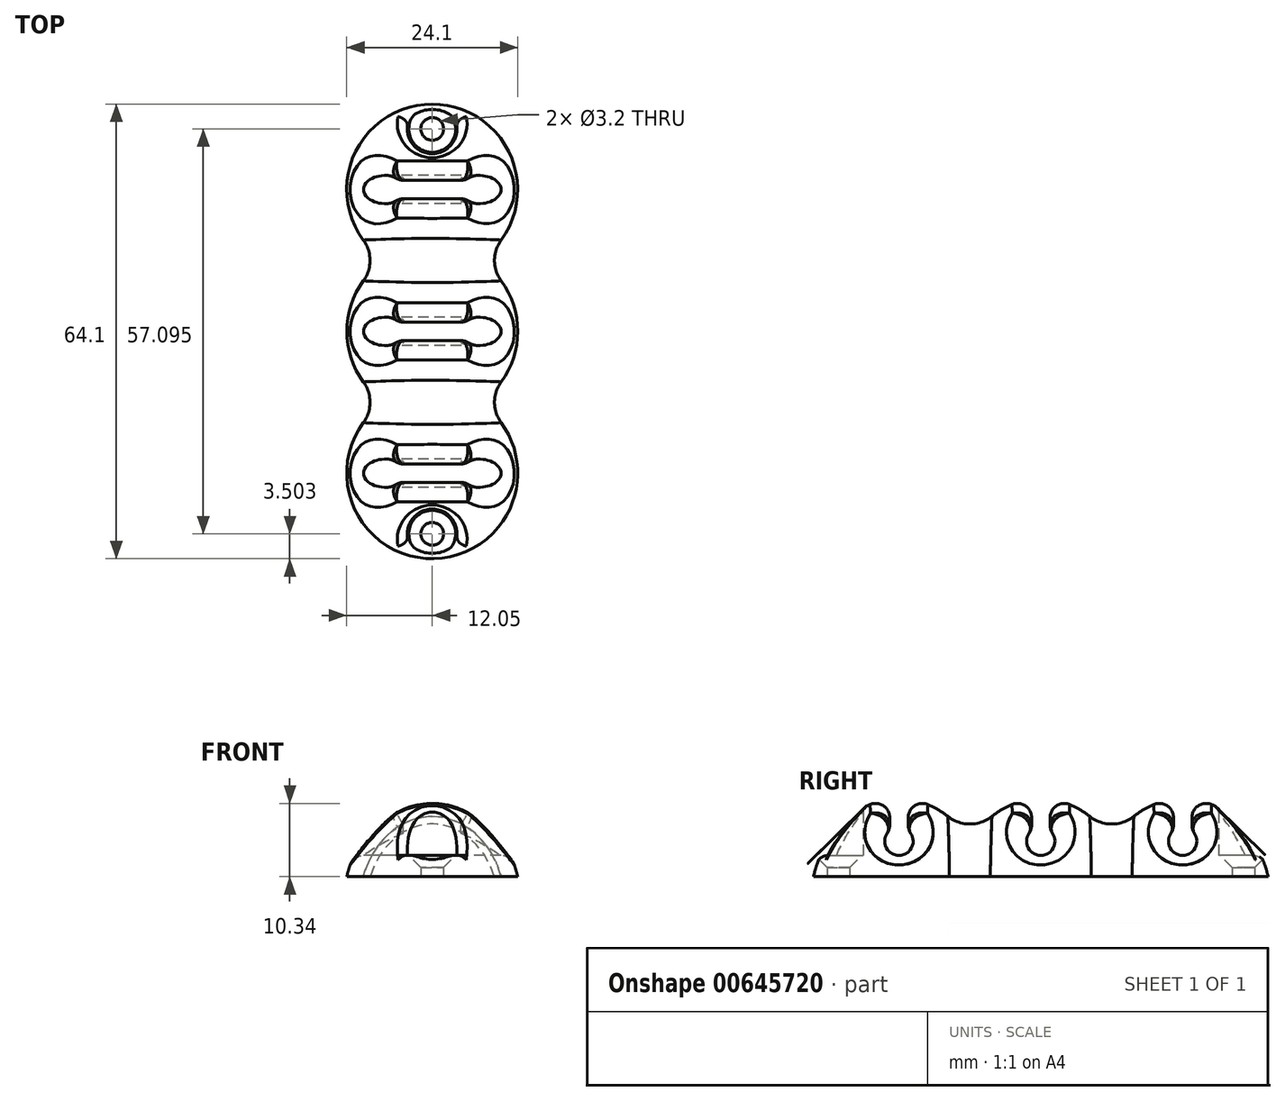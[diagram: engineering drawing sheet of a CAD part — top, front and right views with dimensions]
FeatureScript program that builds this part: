
annotation { "Feature Type Name" : "Feature", "Feature Type Description" : "" }
export const myFeature = defineFeature(function(context is Context, id is Id, definition is map)
    precondition{}
    {
        {
            var Q0;
            Q0=qCreatedBy(makeId("Right.planeOp"),FACE);
            var sketch = newSketch(context, id + "F0", { "sketchPlane" : qUnion([Q0])});
            skEllipse(sketch, "E0", {"center": v(0, -4) * mm, "majorRadius": 12.5 * mm, "minorRadius": 15 * mm, "majorAxis": v(1, 0)});
            skLineSegment(sketch, "E1.bottom", {"start": v(-40.37, 30.12) * mm, "end": v(0, 30.12) * mm});
            skLineSegment(sketch, "E1.top", {"start": v(-40.37, 0) * mm, "end": v(0, 0) * mm});
            skLineSegment(sketch, "E1.left", {"start": v(-40.37, 30.12) * mm, "end": v(-40.37, 0) * mm});
            skLineSegment(sketch, "E1.right", {"start": v(0, 30.12) * mm, "end": v(0, 0) * mm});
            skSolve(sketch);
        }
        {
            var Q0;
            {var subQ0=sQuery(id+"F0.wireOp",EDGE,"E1.top");var subQ1=sQuery(id+"F0.wireOp",EDGE,"E0");var subQ2=makeQuery(id+"F0.imprint","INTERSECT",VERTEX,{"derivedFrom":[subQ1,subQ0]});Q0=makeQuery(id+"F0.imprint","IMPRINT",FACE,{"disambiguationData":[TD([[makeQuery(id+"F0.imprint","IMPRINT",EDGE,{"disambiguationData":[TD([[subQ2,1.0]])],"derivedFrom":subQ1}),1.0]])]});}
            var Q1;
            Q1=sQuery(id+"F0.wireOp",EDGE,"E1.right");
            revolve(context, id + "F1", {"entities" : qUnion([Q0]), "axis" : qUnion([Q1]), "revolveType" : RevolveType.FULL});
        }
        {
            var Q0;
            Q0=qCreatedBy(makeId("Right.planeOp"),FACE);
            var sketch = newSketch(context, id + "F2", { "sketchPlane" : qUnion([Q0])});
            skArc(sketch, "E2", {"start": v(-1.3, 6.52) * mm, "mid": v(0, 3) * mm, "end": v(1.3, 6.52) * mm});
            skLineSegment(sketch, "E3.top", {"start": v(1.3, 24.85) * mm, "end": v(-1.3, 24.85) * mm});
            skLineSegment(sketch, "E3.left", {"start": v(1.3, 6.52) * mm, "end": v(1.3, 24.85) * mm});
            skLineSegment(sketch, "E3.right", {"start": v(-1.3, 6.52) * mm, "end": v(-1.3, 24.85) * mm});
            skPoint(sketch, "E3.middle", {"position": v(0, 15.36) * mm});
            skPoint(sketch, "E4.orphan", {"position": v(-1.3, 5.87) * mm});
            skPoint(sketch, "E5.orphan", {"position": v(1.3, 5.87) * mm});
            skSolve(sketch);
        }
        {
            var Q0;
            Q0=makeQuery(id+"F2.imprint","IMPRINT",FACE,{"disambiguationData":[TD([[makeQuery(id+"F2.imprint","IMPRINT",EDGE,{"derivedFrom":sQuery(id+"F2.wireOp",EDGE,"E2")}),1.0]])]});
            extrude(context, id + "F3", {"entities" : qUnion([Q0]), "depth" : 30 * mm, "offsetDistance" : 25 * mm, "hasSecondDirection" : true, "secondDirectionOppositeDirection" : true, "secondDirectionDepth" : 30 * mm});
        }
        {
            var Q0;
            Q0=makeQuery(id+"F3.opExtrude","SWEPT_EDGE",EDGE,{"disambiguationData":[OSD([sQuery(id+"F2.wireOp",EDGE,"E2"),sQuery(id+"F2.wireOp",EDGE,"E3.right")])]});
            var Q1;
            Q1=makeQuery(id+"F3.opExtrude","SWEPT_EDGE",EDGE,{"disambiguationData":[OSD([sQuery(id+"F2.wireOp",EDGE,"E2"),sQuery(id+"F2.wireOp",EDGE,"E3.left")])]});
            fillet(context, id + "F4", {"entities" : qUnion([Q0, Q1]), "radius" : 2 * mm, "tangentPropagation" : true, "allowEdgeOverflow" : false});
        }
        {
            var Q0;
            Q0=makeQuery(id+"F3.opExtrude","SWEPT_BODY",BODY,{"disambiguationData":[OSD([sQuery(id+"F2.wireOp",EDGE,"E2"),sQuery(id+"F2.wireOp",EDGE,"E3.top"),sQuery(id+"F2.wireOp",EDGE,"E3.left"),sQuery(id+"F2.wireOp",EDGE,"E3.right")])]});
            var Q1;
            Q1=makeQuery(id+"F1.opRevolve","SWEPT_BODY",BODY,{"disambiguationData":[OSD([sQuery(id+"F0.wireOp",EDGE,"E0"),sQuery(id+"F0.wireOp",EDGE,"E1.top"),sQuery(id+"F0.wireOp",EDGE,"E1.right")])]});
            booleanBodies(context, id + "F5", {"operationType" : BooleanOperationType.SUBTRACTION, "tools" : qUnion([Q0]), "targets" : qUnion([Q1])});
        }
        {
            var Q0;
            Q0=makeQuery(id+"F5.opBoolean","INTERSECT",EDGE,{"derivedFrom":[makeQuery(id+"F1.opRevolve","SWEPT_FACE",FACE,{"disambiguationData":[OSD([sQuery(id+"F0.wireOp",EDGE,"E0")])]}),makeQuery(id+"F3.opExtrude","SWEPT_FACE",FACE,{"disambiguationData":[OSD([sQuery(id+"F2.wireOp",EDGE,"E3.right")])]})]});
            fillet(context, id + "F6", {"entities" : qUnion([Q0]), "radius" : 2 * mm, "tangentPropagation" : true, "allowEdgeOverflow" : false});
        }
        {
            var Q0;
            Q0=makeQuery(id+"F1.opRevolve","SWEPT_BODY",BODY,{"disambiguationData":[OSD([sQuery(id+"F0.wireOp",EDGE,"E0"),sQuery(id+"F0.wireOp",EDGE,"E1.top"),sQuery(id+"F0.wireOp",EDGE,"E1.right")])]});
            transform(context, id + "F7", {"entities" : qUnion([Q0]), "transformType" : TransformType.TRANSLATION_3D, "dx" : 0 * mm, "dy" : 20 * mm, "dz" : 0 * mm, "makeCopy" : true});
        }
        {
            var Q0;
            Q0=makeQuery(id+"F7.opPattern","COPY",BODY,{"derivedFrom":makeQuery(id+"F1.opRevolve","SWEPT_BODY",BODY,{"disambiguationData":[OSD([sQuery(id+"F0.wireOp",EDGE,"E0"),sQuery(id+"F0.wireOp",EDGE,"E1.top"),sQuery(id+"F0.wireOp",EDGE,"E1.right")])]}),"instanceName":"1"});
            transform(context, id + "F8", {"entities" : qUnion([Q0]), "transformType" : TransformType.TRANSLATION_3D, "dx" : 0 * mm, "dy" : 20 * mm, "dz" : 0 * mm, "makeCopy" : true});
        }
        {
            var Q0;
            Q0=makeQuery(id+"F1.opRevolve","SWEPT_BODY",BODY,{"disambiguationData":[OSD([sQuery(id+"F0.wireOp",EDGE,"E0"),sQuery(id+"F0.wireOp",EDGE,"E1.top"),sQuery(id+"F0.wireOp",EDGE,"E1.right")])]});
            var Q1;
            Q1=makeQuery(id+"F7.opPattern","COPY",BODY,{"derivedFrom":makeQuery(id+"F1.opRevolve","SWEPT_BODY",BODY,{"disambiguationData":[OSD([sQuery(id+"F0.wireOp",EDGE,"E0"),sQuery(id+"F0.wireOp",EDGE,"E1.top"),sQuery(id+"F0.wireOp",EDGE,"E1.right")])]}),"instanceName":"1"});
            var Q2;
            Q2=makeQuery(id+"F8.opPattern","COPY",BODY,{"derivedFrom":makeQuery(id+"F7.opPattern","COPY",BODY,{"derivedFrom":makeQuery(id+"F1.opRevolve","SWEPT_BODY",BODY,{"disambiguationData":[OSD([sQuery(id+"F0.wireOp",EDGE,"E0"),sQuery(id+"F0.wireOp",EDGE,"E1.top"),sQuery(id+"F0.wireOp",EDGE,"E1.right")])]}),"instanceName":"1"}),"instanceName":"1"});
            booleanBodies(context, id + "F9", {"operationType" : BooleanOperationType.UNION, "tools" : qUnion([Q0, Q1, Q2])});
        }
        {
            var Q0;
            {var subQ0=makeQuery(id+"F1.opRevolve","SWEPT_FACE",FACE,{"disambiguationData":[OSD([sQuery(id+"F0.wireOp",EDGE,"E0")])]});Q0=makeQuery(id+"F9.opBoolean","INTERSECT",EDGE,{"derivedFrom":[subQ0,makeQuery(id+"F7.opPattern","COPY",FACE,{"derivedFrom":subQ0,"instanceName":"1"})]});}
            var Q1;
            {var subQ0=makeQuery(id+"F7.opPattern","COPY",FACE,{"derivedFrom":makeQuery(id+"F1.opRevolve","SWEPT_FACE",FACE,{"disambiguationData":[OSD([sQuery(id+"F0.wireOp",EDGE,"E0")])]}),"instanceName":"1"});Q1=makeQuery(id+"F9.opBoolean","INTERSECT",EDGE,{"derivedFrom":[subQ0,makeQuery(id+"F8.opPattern","COPY",FACE,{"derivedFrom":subQ0,"instanceName":"1"})]});}
            fillet(context, id + "F10", {"entities" : qUnion([Q0, Q1]), "radius" : 5 * mm, "tangentPropagation" : true, "allowEdgeOverflow" : false});
        }
        {
            var Q0;
            {var subQ0=makeQuery(id+"F1.opRevolve","SWEPT_FACE",FACE,{"disambiguationData":[OSD([sQuery(id+"F0.wireOp",EDGE,"E1.top")])]});var subQ1=makeQuery(id+"F7.opPattern","COPY",FACE,{"derivedFrom":subQ0,"instanceName":"1"});Q0=makeQuery(id+"F9.opBoolean","MERGE",FACE,{"derivedFrom":[subQ0,subQ1,makeQuery(id+"F8.opPattern","COPY",FACE,{"derivedFrom":subQ1,"instanceName":"1"})]});}
            var sketch = newSketch(context, id + "F11", { "sketchPlane" : qUnion([Q0])});
            skCircle(sketch, "E6", {"center": v(0, 8.55) * mm, "radius": 3.5 * mm});
            skCircle(sketch, "E7", {"center": v(0, -48.55) * mm, "radius": 3.5 * mm});
            skSolve(sketch);
        }
        {
            var Q0;
            Q0=makeQuery(id+"F11.imprint","IMPRINT",FACE,{"disambiguationData":[TD([[makeQuery(id+"F11.imprint","IMPRINT",EDGE,{"derivedFrom":sQuery(id+"F11.wireOp",EDGE,"E6")}),1.0]])]});
            var Q1;
            Q1=makeQuery(id+"F11.imprint","IMPRINT",FACE,{"disambiguationData":[TD([[makeQuery(id+"F11.imprint","IMPRINT",EDGE,{"derivedFrom":sQuery(id+"F11.wireOp",EDGE,"E7")}),1.0]])]});
            extrude(context, id + "F12", {"entities" : qUnion([Q0, Q1]), "oppositeDirection" : true, "depth" : 25 * mm, "offsetDistance" : 25 * mm});
        }
        {
            var Q0;
            Q0=makeQuery(id+"F12.opExtrude","SWEPT_BODY",BODY,{"disambiguationData":[OSD([sQuery(id+"F11.wireOp",EDGE,"E7")])]});
            var Q1;
            Q1=makeQuery(id+"F12.opExtrude","SWEPT_BODY",BODY,{"disambiguationData":[OSD([sQuery(id+"F11.wireOp",EDGE,"E6")])]});
            transform(context, id + "F13", {"entities" : qUnion([Q0, Q1]), "transformType" : TransformType.TRANSLATION_3D, "dx" : 0 * mm, "dy" : 0 * mm, "dz" : 3 * mm, "makeCopy" : false});
        }
        {
            var Q0;
            Q0=makeQuery(id+"F12.opExtrude","SWEPT_BODY",BODY,{"disambiguationData":[OSD([sQuery(id+"F11.wireOp",EDGE,"E7")])]});
            var Q1;
            Q1=makeQuery(id+"F12.opExtrude","SWEPT_BODY",BODY,{"disambiguationData":[OSD([sQuery(id+"F11.wireOp",EDGE,"E6")])]});
            var Q2;
            Q2=makeQuery(id+"F1.opRevolve","SWEPT_BODY",BODY,{"disambiguationData":[OSD([sQuery(id+"F0.wireOp",EDGE,"E0"),sQuery(id+"F0.wireOp",EDGE,"E1.top"),sQuery(id+"F0.wireOp",EDGE,"E1.right")])]});
            booleanBodies(context, id + "F14", {"operationType" : BooleanOperationType.SUBTRACTION, "tools" : qUnion([Q0, Q1]), "targets" : qUnion([Q2])});
        }
        {
            var Q0;
            Q0=makeQuery(id+"F14.opBoolean","INTERSECT",EDGE,{"derivedFrom":[makeQuery(id+"F8.opPattern","COPY",FACE,{"derivedFrom":makeQuery(id+"F7.opPattern","COPY",FACE,{"derivedFrom":makeQuery(id+"F1.opRevolve","SWEPT_FACE",FACE,{"disambiguationData":[OSD([sQuery(id+"F0.wireOp",EDGE,"E0")])]}),"instanceName":"1"}),"instanceName":"1"}),makeQuery(id+"F12.opExtrude","SWEPT_FACE",FACE,{"disambiguationData":[OSD([sQuery(id+"F11.wireOp",EDGE,"E7")])]})]});
            var Q1;
            Q1=makeQuery(id+"F14.opBoolean","INTERSECT",EDGE,{"derivedFrom":[makeQuery(id+"F8.opPattern","COPY",FACE,{"derivedFrom":makeQuery(id+"F7.opPattern","COPY",FACE,{"derivedFrom":makeQuery(id+"F1.opRevolve","SWEPT_FACE",FACE,{"disambiguationData":[OSD([sQuery(id+"F0.wireOp",EDGE,"E0")])]}),"instanceName":"1"}),"instanceName":"1"}),makeQuery(id+"F12.opExtrude","CAP_FACE",FACE,{"disambiguationData":[OSD([sQuery(id+"F11.wireOp",EDGE,"E7")])],"isStart":true})]});
            var Q2;
            Q2=makeQuery(id+"F14.opBoolean","INTERSECT",EDGE,{"derivedFrom":[makeQuery(id+"F1.opRevolve","SWEPT_FACE",FACE,{"disambiguationData":[OSD([sQuery(id+"F0.wireOp",EDGE,"E0")])]}),makeQuery(id+"F12.opExtrude","SWEPT_FACE",FACE,{"disambiguationData":[OSD([sQuery(id+"F11.wireOp",EDGE,"E6")])]})]});
            var Q3;
            Q3=makeQuery(id+"F14.opBoolean","INTERSECT",EDGE,{"derivedFrom":[makeQuery(id+"F1.opRevolve","SWEPT_FACE",FACE,{"disambiguationData":[OSD([sQuery(id+"F0.wireOp",EDGE,"E0")])]}),makeQuery(id+"F12.opExtrude","CAP_FACE",FACE,{"disambiguationData":[OSD([sQuery(id+"F11.wireOp",EDGE,"E6")])],"isStart":true})]});
            fillet(context, id + "F15", {"entities" : qUnion([Q0, Q1, Q2, Q3]), "radius" : 1 * mm, "tangentPropagation" : true, "allowEdgeOverflow" : false});
        }
        {
            var Q0;
            {var subQ0=makeQuery(id+"F1.opRevolve","SWEPT_FACE",FACE,{"disambiguationData":[OSD([sQuery(id+"F0.wireOp",EDGE,"E1.top")])]});var subQ1=makeQuery(id+"F7.opPattern","COPY",FACE,{"derivedFrom":subQ0,"instanceName":"1"});Q0=makeQuery(id+"F9.opBoolean","MERGE",FACE,{"derivedFrom":[subQ0,subQ1,makeQuery(id+"F8.opPattern","COPY",FACE,{"derivedFrom":subQ1,"instanceName":"1"})]});}
            var sketch = newSketch(context, id + "F16", { "sketchPlane" : qUnion([Q0])});
            skCircle(sketch, "E8", {"center": v(0, 8.55) * mm, "radius": 1.6 * mm});
            skCircle(sketch, "E9", {"center": v(0, -48.55) * mm, "radius": 1.6 * mm});
            skSolve(sketch);
        }
        {
            var Q0;
            Q0=makeQuery(id+"F16.imprint","IMPRINT",FACE,{"disambiguationData":[TD([[makeQuery(id+"F16.imprint","IMPRINT",EDGE,{"derivedFrom":sQuery(id+"F16.wireOp",EDGE,"E8")}),1.0]])]});
            var Q1;
            Q1=makeQuery(id+"F16.imprint","IMPRINT",FACE,{"disambiguationData":[TD([[makeQuery(id+"F16.imprint","IMPRINT",EDGE,{"derivedFrom":sQuery(id+"F16.wireOp",EDGE,"E9")}),1.0]])]});
            extrude(context, id + "F17", {"entities" : qUnion([Q0, Q1]), "operationType" : NewBodyOperationType.REMOVE, "endBound" : BoundingType.THROUGH_ALL, "oppositeDirection" : true, "depth" : 25 * mm, "offsetDistance" : 25 * mm});
        }
        {
            var Q0;
            Q0=makeQuery(id+"F17.boolean.opBoolean","INTERSECT",EDGE,{"derivedFrom":[makeQuery(id+"F14.opBoolean","COPY",FACE,{"derivedFrom":makeQuery(id+"F12.opExtrude","CAP_FACE",FACE,{"disambiguationData":[OSD([sQuery(id+"F11.wireOp",EDGE,"E6")])],"isStart":true})}),makeQuery(id+"F17.opExtrude","SWEPT_FACE",FACE,{"disambiguationData":[OSD([sQuery(id+"F16.wireOp",EDGE,"E8")])]})]});
            var Q1;
            Q1=makeQuery(id+"F17.boolean.opBoolean","INTERSECT",EDGE,{"derivedFrom":[makeQuery(id+"F14.opBoolean","COPY",FACE,{"derivedFrom":makeQuery(id+"F12.opExtrude","CAP_FACE",FACE,{"disambiguationData":[OSD([sQuery(id+"F11.wireOp",EDGE,"E7")])],"isStart":true})}),makeQuery(id+"F17.opExtrude","SWEPT_FACE",FACE,{"disambiguationData":[OSD([sQuery(id+"F16.wireOp",EDGE,"E9")])]})]});
            chamfer(context, id + "F18", {"entities" : qUnion([Q0, Q1]), "width" : 1.7 * mm, "tangentPropagation" : true});
        }
    });
